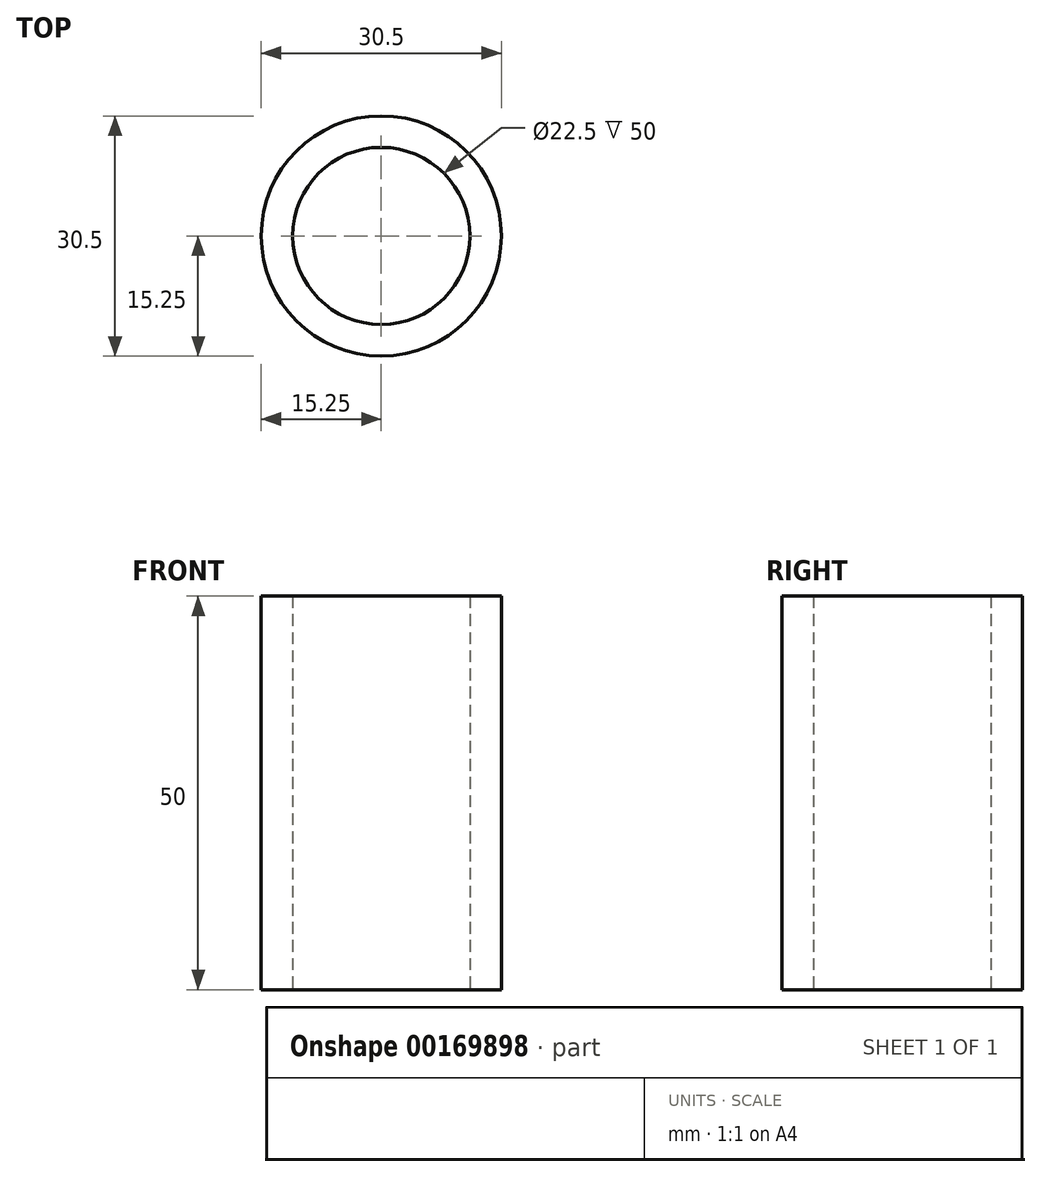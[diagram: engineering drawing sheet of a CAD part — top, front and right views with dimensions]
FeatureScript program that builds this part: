
annotation { "Feature Type Name" : "Feature", "Feature Type Description" : "" }
export const myFeature = defineFeature(function(context is Context, id is Id, definition is map)
    precondition{}
    {
        {
            var Q0;
            Q0=qCreatedBy(makeId("Top.planeOp"),FACE);
            var sketch = newSketch(context, id + "F0", { "sketchPlane" : qUnion([Q0])});
            skCircle(sketch, "E0", {"center": v(0, 0) * mm, "radius": 11.25 * mm});
            skCircle(sketch, "E1", {"center": v(0, 0) * mm, "radius": 15.25 * mm});
            skSolve(sketch);
        }
        {
            var Q0;
            Q0=makeQuery(id+"F0.imprint","IMPRINT",FACE,{"disambiguationData":[TD([[makeQuery(id+"F0.imprint","IMPRINT",EDGE,{"derivedFrom":sQuery(id+"F0.wireOp",EDGE,"E0")}),-1.0]])]});
            extrude(context, id + "F1", {"entities" : qUnion([Q0]), "depth" : 50 * mm});
        }
    });
